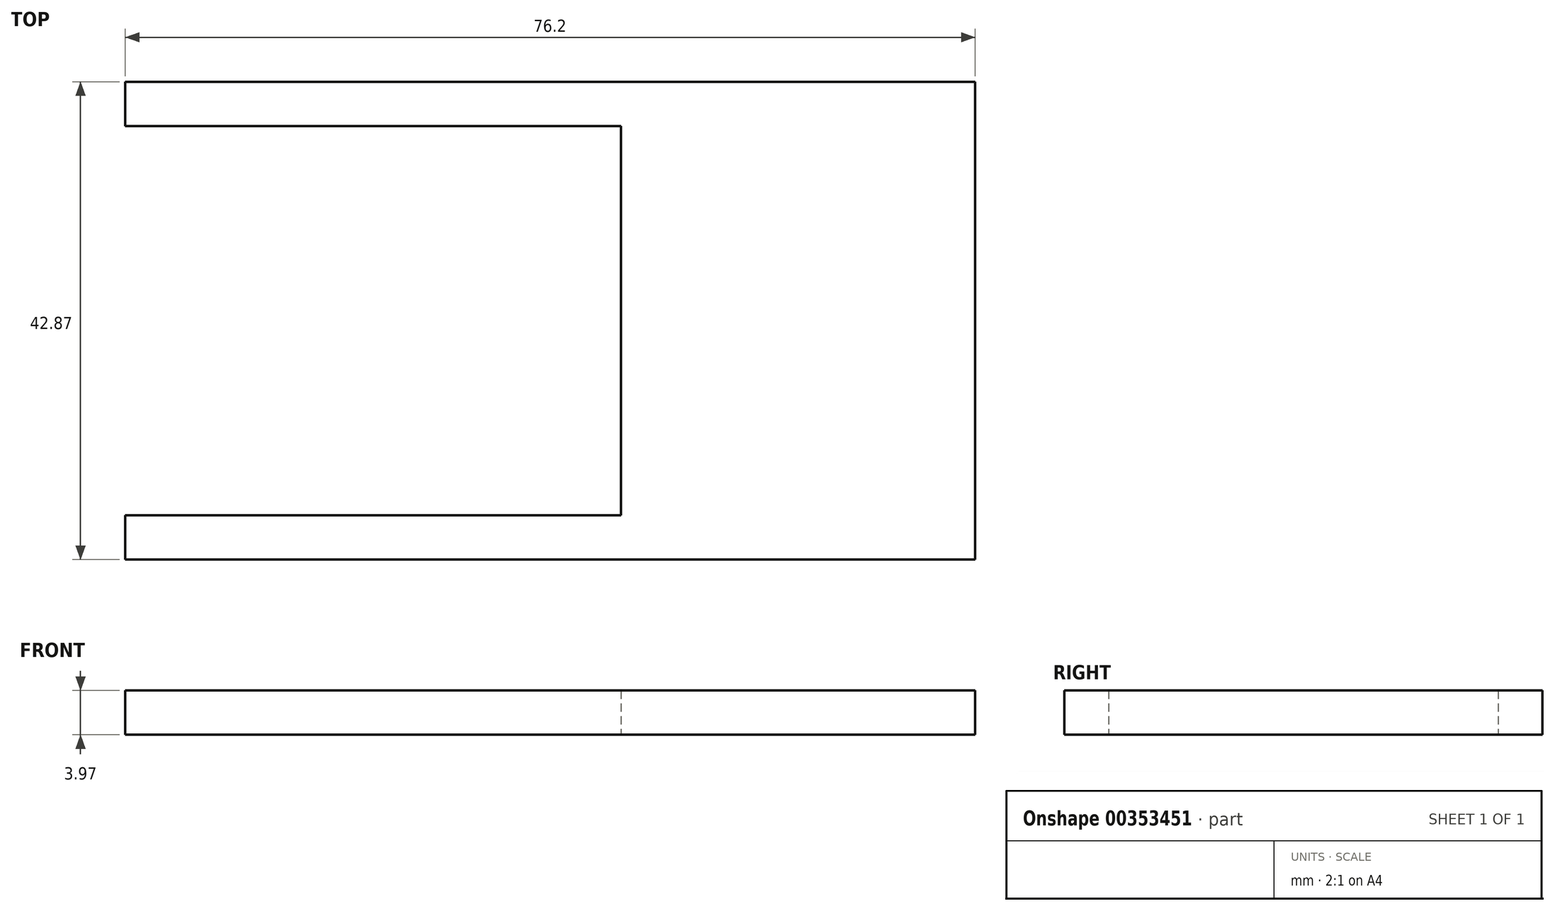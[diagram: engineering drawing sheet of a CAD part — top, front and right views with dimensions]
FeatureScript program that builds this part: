
annotation { "Feature Type Name" : "Feature", "Feature Type Description" : "" }
export const myFeature = defineFeature(function(context is Context, id is Id, definition is map)
    precondition{}
    {
        {
            var Q0;
            Q0=qCreatedBy(makeId("Top.planeOp"),FACE);
            var sketch = newSketch(context, id + "F0", { "sketchPlane" : qUnion([Q0])});
            skLineSegment(sketch, "E0.bottom", {"start": v(-37.71, -11.68) * mm, "end": v(38.49, -11.68) * mm});
            skLineSegment(sketch, "E0.top", {"start": v(-37.71, 31.19) * mm, "end": v(38.49, 31.19) * mm});
            skLineSegment(sketch, "E0.left", {"start": v(-37.71, -11.68) * mm, "end": v(-37.71, 31.19) * mm});
            skLineSegment(sketch, "E0.right", {"start": v(38.49, -11.68) * mm, "end": v(38.49, 31.19) * mm});
            skLineSegment(sketch, "E1", {"start": v(-37.71, 31.19) * mm, "end": v(-37.71, 27.22) * mm});
            skLineSegment(sketch, "E2", {"start": v(-37.71, -11.68) * mm, "end": v(-37.71, -7.7) * mm});
            skLineSegment(sketch, "E3", {"start": v(-37.71, 27.22) * mm, "end": v(6.73, 27.22) * mm});
            skLineSegment(sketch, "E4", {"start": v(-37.71, -7.7) * mm, "end": v(6.73, -7.7) * mm});
            skLineSegment(sketch, "E5", {"start": v(6.73, -7.7) * mm, "end": v(6.73, 27.22) * mm});
            skSolve(sketch);
        }
        {
            var Q0;
            Q0=makeQuery(id+"F0.imprint","IMPRINT",FACE,{"disambiguationData":[TD([[makeQuery(id+"F0.imprint","IMPRINT",EDGE,{"derivedFrom":sQuery(id+"F0.wireOp",EDGE,"E0.bottom")}),1.0]])]});
            extrude(context, id + "F1", {"entities" : qUnion([Q0]), "depth" : 3.97 * mm});
        }
    });
